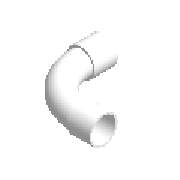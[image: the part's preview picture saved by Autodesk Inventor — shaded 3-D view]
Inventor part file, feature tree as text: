
AUTODESK INVENTOR PART (.ipt)
format: ipt  version: 2023 (Build 270158000, 158)  size: 221,696 bytes
history: native  units: mm (DEFAULTED — no unit token found)
features: other x6, sketch x2, revolve x2, sweep x1
ambient origin geometry x8: Origin, YZ Plane, XZ Plane, XY Plane, X Axis, Y Axis, Z Axis, Center Point
bodies: Solid1 (feature_tree)
feature tree (11):
  sketch  "Sketch1"  dims[d3=90.0deg d0=40.0mm]
  revolve  "Revolution1"  [1 undecoded]
  sweep  "Sweep1"
  revolve  "Revolution2"  [1 undecoded]
  other  "Work Point18"
  other  "Work Point19"
  other  "Work Axis30"
  other  "Work Point20"
  other  "Work Axis31"
  other  "Work Point21"
  sketch  "Sketch2"  dims[d1=3.0mm d2=26.0mm d4=34.0mm d5=0.0mm d6=40.0mm d7=34.0mm d8=77.0mm d9=77.0mm d160=90.0deg d10=3.0mm d11=3.0mm d12=26.0mm d13=40.0mm d14=80.0mm d15=80.0mm d16=3.0mm d192=0.0mm]
note: 2 required parameter values undecoded (feature->parameter linkage not recoverable at this tier; creation-order binding heuristic only, values carry confidence <= 0.55)
